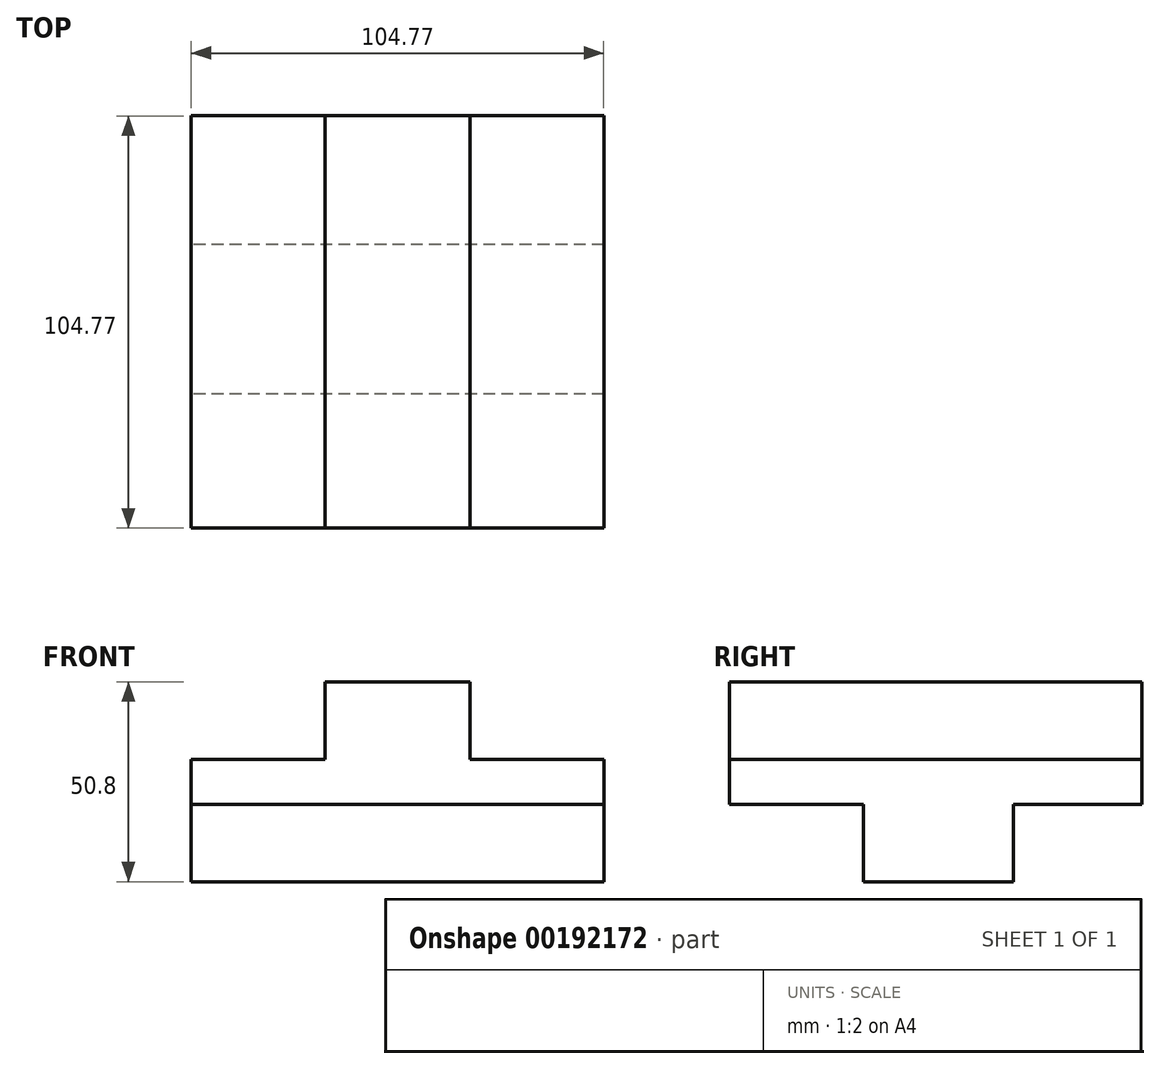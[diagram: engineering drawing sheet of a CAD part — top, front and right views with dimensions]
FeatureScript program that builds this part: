
annotation { "Feature Type Name" : "Feature", "Feature Type Description" : "" }
export const myFeature = defineFeature(function(context is Context, id is Id, definition is map)
    precondition{}
    {
        {
            var Q0;
            Q0=qCreatedBy(makeId("Top.planeOp"),FACE);
            var sketch = newSketch(context, id + "F0", { "sketchPlane" : qUnion([Q0])});
            skLineSegment(sketch, "E0.bottom", {"start": v(0, 0) * mm, "end": v(104.78, 0) * mm});
            skLineSegment(sketch, "E0.top", {"start": v(0, 104.78) * mm, "end": v(104.77, 104.78) * mm});
            skLineSegment(sketch, "E0.left", {"start": v(0, 0) * mm, "end": v(0, 104.78) * mm});
            skLineSegment(sketch, "E0.right", {"start": v(104.78, 0) * mm, "end": v(104.77, 104.78) * mm});
            skSolve(sketch);
        }
        {
            var Q0;
            Q0=makeQuery(id+"F0.imprint","IMPRINT",FACE,{"disambiguationData":[TD([[makeQuery(id+"F0.imprint","IMPRINT",EDGE,{"derivedFrom":sQuery(id+"F0.wireOp",EDGE,"E0.bottom")}),1.0]])]});
            extrude(context, id + "F1", {"entities" : qUnion([Q0]), "depth" : 50.8 * mm});
        }
        {
            var Q0;
            Q0=makeQuery(id+"F1.opExtrude","SWEPT_FACE",FACE,{"disambiguationData":[OSD([sQuery(id+"F0.wireOp",EDGE,"E0.bottom")])]});
            var sketch = newSketch(context, id + "F2", { "sketchPlane" : qUnion([Q0])});
            skLineSegment(sketch, "E1.bottom", {"start": v(104.78, 50.8) * mm, "end": v(70.74, 50.8) * mm});
            skLineSegment(sketch, "E1.top", {"start": v(104.78, 31.12) * mm, "end": v(70.74, 31.12) * mm});
            skLineSegment(sketch, "E1.left", {"start": v(104.78, 50.8) * mm, "end": v(104.78, 31.12) * mm});
            skLineSegment(sketch, "E1.right", {"start": v(70.74, 50.8) * mm, "end": v(70.74, 31.12) * mm});
            skLineSegment(sketch, "E2.bottom", {"start": v(0, 50.8) * mm, "end": v(34.04, 50.8) * mm});
            skLineSegment(sketch, "E2.top", {"start": v(0, 31.12) * mm, "end": v(34.04, 31.12) * mm});
            skLineSegment(sketch, "E2.left", {"start": v(0, 50.8) * mm, "end": v(0, 31.12) * mm});
            skLineSegment(sketch, "E2.right", {"start": v(34.04, 50.8) * mm, "end": v(34.04, 31.11) * mm});
            skSolve(sketch);
        }
        {
            var Q0;
            Q0=makeQuery(id+"F2.imprint","IMPRINT",FACE,{"disambiguationData":[TD([[makeQuery(id+"F2.imprint","IMPRINT",EDGE,{"derivedFrom":sQuery(id+"F2.wireOp",EDGE,"E1.bottom")}),-1.0]])]});
            var Q1;
            Q1=makeQuery(id+"F2.imprint","IMPRINT",FACE,{"disambiguationData":[TD([[makeQuery(id+"F2.imprint","IMPRINT",EDGE,{"derivedFrom":sQuery(id+"F2.wireOp",EDGE,"E2.bottom")}),-1.0]])]});
            extrude(context, id + "F3", {"entities" : qUnion([Q0, Q1]), "operationType" : NewBodyOperationType.REMOVE, "oppositeDirection" : true, "depth" : 104.77 * mm});
        }
        {
            var Q0;
            Q0=qCreatedBy(makeId("Right.planeOp"),FACE);
            var sketch = newSketch(context, id + "F4", { "sketchPlane" : qUnion([Q0])});
            skLineSegment(sketch, "E3.bottom", {"start": v(0, 0) * mm, "end": v(34.04, 0) * mm});
            skLineSegment(sketch, "E3.top", {"start": v(0, 19.69) * mm, "end": v(34.04, 19.69) * mm});
            skLineSegment(sketch, "E3.left", {"start": v(0, 0) * mm, "end": v(0, 19.69) * mm});
            skLineSegment(sketch, "E3.right", {"start": v(34.04, 0) * mm, "end": v(34.04, 19.69) * mm});
            skLineSegment(sketch, "E4.bottom", {"start": v(106.1, 0) * mm, "end": v(72.06, 0) * mm});
            skLineSegment(sketch, "E4.top", {"start": v(106.1, 19.69) * mm, "end": v(72.06, 19.69) * mm});
            skLineSegment(sketch, "E4.left", {"start": v(106.1, 0) * mm, "end": v(106.1, 19.69) * mm});
            skLineSegment(sketch, "E4.right", {"start": v(72.06, 0) * mm, "end": v(72.06, 19.69) * mm});
            skSolve(sketch);
        }
        {
            var Q0;
            Q0=makeQuery(id+"F4.imprint","IMPRINT",FACE,{"disambiguationData":[TD([[makeQuery(id+"F4.imprint","IMPRINT",EDGE,{"derivedFrom":sQuery(id+"F4.wireOp",EDGE,"E4.bottom")}),-1.0]])]});
            var Q1;
            Q1=makeQuery(id+"F4.imprint","IMPRINT",FACE,{"disambiguationData":[TD([[makeQuery(id+"F4.imprint","IMPRINT",EDGE,{"derivedFrom":sQuery(id+"F4.wireOp",EDGE,"E3.bottom")}),1.0]])]});
            extrude(context, id + "F5", {"entities" : qUnion([Q0, Q1]), "operationType" : NewBodyOperationType.REMOVE, "depth" : 158.24 * mm});
        }
    });
